# Revit family: Vitra-SinkMixer-OriginSeries-A42559
name_source: partatom
category: Plumbing Fixtures
revit_build: Autodesk Revit 2017 (Build: 20160225_1515(x64)
units: mm (PartAtom-declared; Revit-internal decimal feet)

## family parameters
Cut with Voids When Loaded = No
Host = Face
OmniClass Number = 23.45.55.17
OmniClass Title = Mixing Faucets
Part Type = Normal
Room Calculation Point = No
Round Connector Dimension = Use Diameter
Shared = Yes

## types (4) — shared parameters
BIMobject category = Sink Mixer
CW Connection = Yes
Connection Diameter (mm) = 10 mm  [stored 0.0328084 ft]
Default Elevation = 850 mm  [stored 2.78871 ft]
Depth(mm) = 134 mm
Description = To clean your product use a soft cloth soaked in alcohol or soap. Never use. acid or hydrochloric acid used to clean closed and floor and never use cleaning salt used to clean basin and sink.
Design country = Turkey
HW Connection = Yes
Height(mm) = 171 mm  [stored 0.561024 ft]
Hot Water Supply (max.) = 80 °C
Hot Water temperature, factory set to = 38 °C
IFC Classification = Sanitary Terminal
Installation instructions = file://ygbzfilesrv/ArtemaBarcod/Attach/A79558.pdf
Main Material = Brass
Manufacturer = Vitra
Manufacturer name = Vitra
Masterformat 2014 Code = 22 40 00
Masterformat 2014 Description = Plumbing Fixtures
Min. flow pressure of = 0.5 bar
MountingType = Countertop
NBS Referans Code = 45-35-70/345
NBS Referans Description = Water supply fittings for sinks
Nominal height = 0.000
Nominal width = 0.000
Number Of Connections = 2 mm  [stored 0.00656168 ft]
OmniClass Code = 23.45.55.17
OmniClass Description = Mixing Faucets
Product Guid = file://ygbzfilesrv/ArtemaBarcod/Attach/A79491.pdf
Product Properties = Extra Water Saving, Green Building Certification, Energy Saving, Easy İnstallation
Product Type = Sink Mixer
Product certification = https://vitraglobal.com
Product data url = https://www.vitra.com.tr
Product family = Origin
Product group = Origin Sink Mixer
Range of Hot Water Supply = 5 - 65 °C
Range of flow pressure = 1 - 5 bar
Technical description = https://www.vitra.com.tr
Test Pressure = 16 bar
UNSPSC Code = 301815
URL = https://vitraglobal.com
Uniclass 1.4 Code = L725111
Uniclass 1.4 Description = Sink Mixer
Uniclass 2.0 Code = Pr_40_30_96_47
Uniclass 2.0 Description = Kitchen Taps
Uniclass 2015 Code = Pr_40_20_87_84
Uniclass 2015 Name = Sink taps
Uniformat II Code = 22 40 00
Uniformat II Description = Plumbing Fixture
Warranty Period (Year) = 10 Years
Weight Net (kg) = 1.960
Width(mm) = 58 mm  [stored 0.190289 ft]
Youtube = https://www.youtube.com
zero-valued in all types: Cost

## per-type parameters (varying)
| type | Article No. (default) | Coating Material | Color | Model | Product SKU |
| SinkMixer-Vitra-OriginSeries(Chrome)-A42559 | A42559 | Vitra-Chrome | Chrome | A42559 | A42559 |
| SinkMixer-Vitra-OriginSeries(BrightCopper)-A4255926 | A4255926 | Vitra-BrightCopper | Bright Copper | A4255926 | A4255926 |
| SinkMixer-Vitra-OriginSeries(Nickel)-A4255934 | A4255934 | Vitra-Nickel | Nickel | A4255934 | A4255934 |
| SinkMixer-Vitra-OriginSeries(MatteBlack)-A4255936 | A4255936 | Vitra-MatteBlack | Matte Black | A4255936 | A4255936 |

note: [stored X ft] marks values corroborated as IEEE doubles in the binary element streams (Revit-internal decimal feet)

## geometry (parser evidence)
native form markers: Sweep x3
no freeform markers — native parametric forms only
